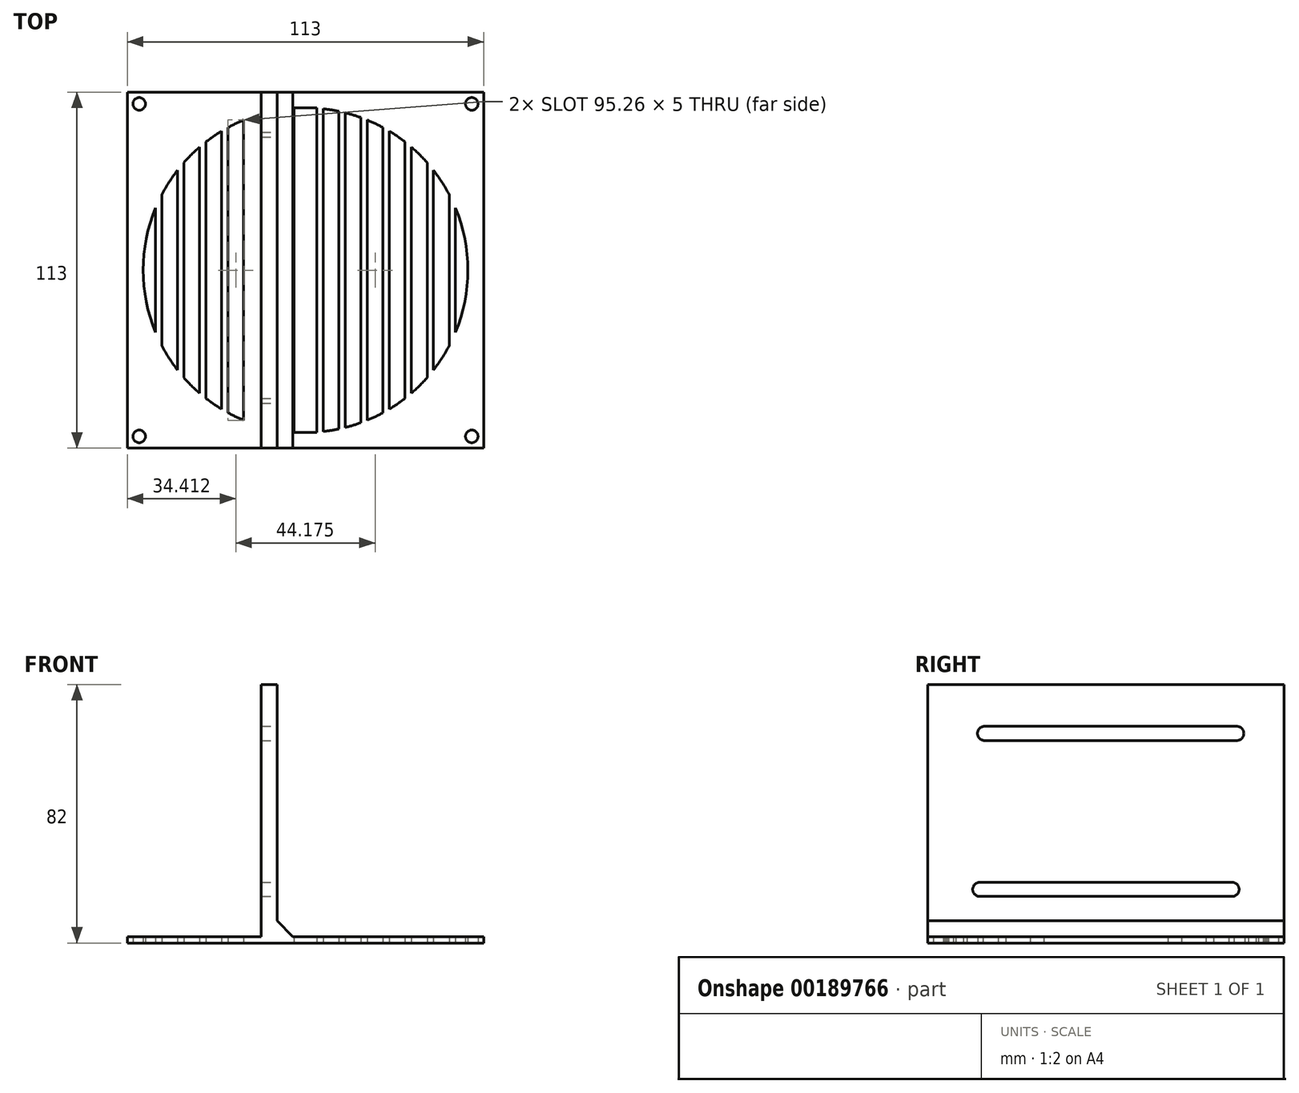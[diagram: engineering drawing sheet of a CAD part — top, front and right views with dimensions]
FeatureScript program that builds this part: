
annotation { "Feature Type Name" : "Feature", "Feature Type Description" : "" }
export const myFeature = defineFeature(function(context is Context, id is Id, definition is map)
    precondition{}
    {
        {
            var Q0;
            Q0=qCreatedBy(makeId("Top.planeOp"),FACE);
            var sketch = newSketch(context, id + "F0", { "sketchPlane" : qUnion([Q0])});
            skLineSegment(sketch, "E0.bottom", {"start": v(56.5, 56.5) * mm, "end": v(-56.5, 56.5) * mm});
            skLineSegment(sketch, "E0.top", {"start": v(56.5, -56.5) * mm, "end": v(-56.5, -56.5) * mm});
            skLineSegment(sketch, "E0.left", {"start": v(56.5, 56.5) * mm, "end": v(56.5, -56.5) * mm});
            skLineSegment(sketch, "E0.right", {"start": v(-56.5, 56.5) * mm, "end": v(-56.5, -56.5) * mm});
            skPoint(sketch, "E0.middle", {"position": v(0, 0) * mm});
            skCircle(sketch, "E1", {"center": v(-52.75, 52.75) * mm, "radius": 2 * mm});
            skCircle(sketch, "E2", {"center": v(52.75, 52.75) * mm, "radius": 2 * mm});
            skCircle(sketch, "E3", {"center": v(52.75, -52.75) * mm, "radius": 2 * mm});
            skCircle(sketch, "E4", {"center": v(-52.75, -52.75) * mm, "radius": 2 * mm});
            skLineSegment(sketch, "E5", {"start": v(-47.59, 19.69) * mm, "end": v(-47.59, -19.69) * mm});
            skLineSegment(sketch, "E6", {"start": v(-45.59, 23.96) * mm, "end": v(-45.59, -23.96) * mm});
            skLineSegment(sketch, "E7", {"start": v(-40.59, 31.7) * mm, "end": v(-40.59, -31.7) * mm});
            skLineSegment(sketch, "E8", {"start": v(-38.59, 34.1) * mm, "end": v(-38.59, -34.1) * mm});
            skLineSegment(sketch, "E9", {"start": v(-33.59, 39.04) * mm, "end": v(-33.59, -39.04) * mm});
            skLineSegment(sketch, "E10", {"start": v(-31.59, 40.68) * mm, "end": v(-31.59, -40.68) * mm});
            skLineSegment(sketch, "E11", {"start": v(-26.59, 44.1) * mm, "end": v(-26.59, -44.1) * mm});
            skLineSegment(sketch, "E12", {"start": v(-24.59, 45.25) * mm, "end": v(-24.59, -45.25) * mm});
            skLineSegment(sketch, "E13", {"start": v(-19.59, 47.63) * mm, "end": v(-19.59, -47.63) * mm});
            skLineSegment(sketch, "E14", {"start": v(-17.59, 48.4) * mm, "end": v(-17.59, -48.4) * mm});
            skLineSegment(sketch, "E15", {"start": v(-5.59, -51.2) * mm, "end": v(-5.59, 51.2) * mm});
            skLineSegment(sketch, "E16", {"start": v(0, 51.5) * mm, "end": v(0, -51.5) * mm});
            skPoint(sketch, "E16.endSnap0", {"position": v(0, -56.5) * mm});
            skArc(sketch, "E17.trimOffspring", {"start": v(-47.59, 19.69) * mm, "mid": v(-51.5, 0) * mm, "end": v(-47.59, -19.69) * mm});
            skArc(sketch, "E18.trimOffspring", {"start": v(-40.59, 31.7) * mm, "mid": v(-43.26, 27.94) * mm, "end": v(-45.59, 23.96) * mm});
            skArc(sketch, "E19.trimOffspring", {"start": v(-33.59, 39.04) * mm, "mid": v(-36.17, 36.66) * mm, "end": v(-38.59, 34.1) * mm});
            skArc(sketch, "E20.trimOffspring", {"start": v(-26.59, 44.1) * mm, "mid": v(-29.14, 42.46) * mm, "end": v(-31.59, 40.68) * mm});
            skArc(sketch, "E21.trimOffspring", {"start": v(-19.59, 47.63) * mm, "mid": v(-22.12, 46.5) * mm, "end": v(-24.59, 45.25) * mm});
            skArc(sketch, "E22.trimOffspring", {"start": v(-24.59, -45.25) * mm, "mid": v(-22.12, -46.5) * mm, "end": v(-19.59, -47.63) * mm});
            skArc(sketch, "E23.trimOffspring", {"start": v(-31.59, -40.68) * mm, "mid": v(-29.14, -42.46) * mm, "end": v(-26.59, -44.1) * mm});
            skArc(sketch, "E24.trimOffspring", {"start": v(-38.59, -34.1) * mm, "mid": v(-36.17, -36.66) * mm, "end": v(-33.59, -39.04) * mm});
            skArc(sketch, "E25.trimOffspring", {"start": v(-45.59, -23.96) * mm, "mid": v(-43.26, -27.94) * mm, "end": v(-40.59, -31.7) * mm});
            skArc(sketch, "E26.MirrorCS", {"start": v(26.59, 44.1) * mm, "mid": v(29.14, 42.46) * mm, "end": v(31.59, 40.68) * mm});
            skArc(sketch, "E27.MirrorCS", {"start": v(24.59, -45.25) * mm, "mid": v(22.12, -46.5) * mm, "end": v(19.59, -47.63) * mm});
            skArc(sketch, "E28.MirrorCS", {"start": v(33.59, 39.04) * mm, "mid": v(36.17, 36.66) * mm, "end": v(38.59, 34.1) * mm});
            skArc(sketch, "E29.MirrorCS", {"start": v(38.59, -34.1) * mm, "mid": v(36.17, -36.66) * mm, "end": v(33.59, -39.04) * mm});
            skArc(sketch, "E30.MirrorCS", {"start": v(17.59, -48.4) * mm, "mid": v(15.1, -49.23) * mm, "end": v(12.59, -49.94) * mm});
            skArc(sketch, "E31.MirrorCS", {"start": v(5.59, 51.2) * mm, "mid": v(8.1, 50.86) * mm, "end": v(10.59, 50.4) * mm});
            skArc(sketch, "E32.MirrorCS", {"start": v(10.59, -50.4) * mm, "mid": v(8.1, -50.86) * mm, "end": v(5.59, -51.2) * mm});
            skArc(sketch, "E33.MirrorCS", {"start": v(12.59, 49.94) * mm, "mid": v(15.1, 49.23) * mm, "end": v(17.59, 48.4) * mm});
            skArc(sketch, "E34.MirrorCS", {"start": v(31.59, -40.68) * mm, "mid": v(29.14, -42.46) * mm, "end": v(26.59, -44.1) * mm});
            skArc(sketch, "E35.MirrorCS", {"start": v(19.59, 47.63) * mm, "mid": v(22.12, 46.5) * mm, "end": v(24.59, 45.25) * mm});
            skArc(sketch, "E36.MirrorCS", {"start": v(45.59, -23.96) * mm, "mid": v(43.26, -27.94) * mm, "end": v(40.59, -31.7) * mm});
            skLineSegment(sketch, "E37.MirrorCS", {"start": v(12.59, 49.94) * mm, "end": v(12.59, -49.94) * mm});
            skLineSegment(sketch, "E38.MirrorCS", {"start": v(17.59, 48.4) * mm, "end": v(17.59, -48.4) * mm});
            skLineSegment(sketch, "E39.MirrorCS", {"start": v(33.59, 39.04) * mm, "end": v(33.59, -39.04) * mm});
            skLineSegment(sketch, "E40.MirrorCS", {"start": v(31.59, 40.68) * mm, "end": v(31.59, -40.68) * mm});
            skLineSegment(sketch, "E41.MirrorCS", {"start": v(26.59, 44.1) * mm, "end": v(26.59, -44.1) * mm});
            skLineSegment(sketch, "E42.MirrorCS", {"start": v(38.59, 34.1) * mm, "end": v(38.59, -34.1) * mm});
            skLineSegment(sketch, "E43.MirrorCS", {"start": v(40.59, 31.7) * mm, "end": v(40.59, -31.7) * mm});
            skLineSegment(sketch, "E44.MirrorCS", {"start": v(45.59, 23.96) * mm, "end": v(45.59, -23.96) * mm});
            skLineSegment(sketch, "E45.MirrorCS", {"start": v(47.59, 19.69) * mm, "end": v(47.59, -19.69) * mm});
            skLineSegment(sketch, "E46.MirrorCS", {"start": v(5.59, -51.2) * mm, "end": v(5.59, 51.2) * mm});
            skLineSegment(sketch, "E47.MirrorCS", {"start": v(19.59, 47.63) * mm, "end": v(19.59, -47.63) * mm});
            skArc(sketch, "E48.MirrorCS", {"start": v(40.59, 31.7) * mm, "mid": v(43.26, 27.94) * mm, "end": v(45.59, 23.96) * mm});
            skLineSegment(sketch, "E49.MirrorCS", {"start": v(10.59, 50.4) * mm, "end": v(10.59, -50.4) * mm});
            skLineSegment(sketch, "E50.MirrorCS", {"start": v(24.59, 45.25) * mm, "end": v(24.59, -45.25) * mm});
            skArc(sketch, "E51.MirrorCS", {"start": v(47.59, 19.69) * mm, "mid": v(51.5, 0) * mm, "end": v(47.59, -19.69) * mm});
            skLineSegment(sketch, "E52.bottom", {"start": v(-3.59, 51.52) * mm, "end": v(3.59, 51.52) * mm});
            skLineSegment(sketch, "E52.top", {"start": v(-3.59, -51.52) * mm, "end": v(3.59, -51.52) * mm});
            skLineSegment(sketch, "E52.left", {"start": v(-3.59, 51.52) * mm, "end": v(-3.59, -51.52) * mm});
            skLineSegment(sketch, "E52.right", {"start": v(3.59, 51.52) * mm, "end": v(3.59, -51.52) * mm});
            skSolve(sketch);
        }
        {
            var Q0;
            Q0=makeQuery(id+"F0.imprint","IMPRINT",FACE,{"disambiguationData":[TD([[makeQuery(id+"F0.imprint","IMPRINT",EDGE,{"derivedFrom":sQuery(id+"F0.wireOp",EDGE,"E0.bottom")}),1.0]])]});
            extrude(context, id + "F1", {"entities" : qUnion([Q0]), "depth" : 2 * mm});
        }
        {
            var Q0;
            Q0=makeQuery(id+"F1.opExtrude","CAP_FACE",FACE,{"disambiguationData":[OSD([sQuery(id+"F0.wireOp",EDGE,"E0.bottom"),sQuery(id+"F0.wireOp",EDGE,"E0.top"),sQuery(id+"F0.wireOp",EDGE,"E0.left"),sQuery(id+"F0.wireOp",EDGE,"E0.right"),sQuery(id+"F0.wireOp",EDGE,"E1"),sQuery(id+"F0.wireOp",EDGE,"E3"),sQuery(id+"F0.wireOp",EDGE,"E4"),sQuery(id+"F0.wireOp",EDGE,"E5"),sQuery(id+"F0.wireOp",EDGE,"E6"),sQuery(id+"F0.wireOp",EDGE,"E7"),sQuery(id+"F0.wireOp",EDGE,"E8"),sQuery(id+"F0.wireOp",EDGE,"E9"),sQuery(id+"F0.wireOp",EDGE,"E10"),sQuery(id+"F0.wireOp",EDGE,"E11"),sQuery(id+"F0.wireOp",EDGE,"E12"),sQuery(id+"F0.wireOp",EDGE,"E13"),sQuery(id+"F0.wireOp",EDGE,"E17.trimOffspring"),sQuery(id+"F0.wireOp",EDGE,"E18.trimOffspring"),sQuery(id+"F0.wireOp",EDGE,"E19.trimOffspring"),sQuery(id+"F0.wireOp",EDGE,"E20.trimOffspring"),sQuery(id+"F0.wireOp",EDGE,"E21.trimOffspring"),sQuery(id+"F0.wireOp",EDGE,"E22.trimOffspring"),sQuery(id+"F0.wireOp",EDGE,"E23.trimOffspring"),sQuery(id+"F0.wireOp",EDGE,"E24.trimOffspring"),sQuery(id+"F0.wireOp",EDGE,"E25.trimOffspring"),sQuery(id+"F0.wireOp",EDGE,"E26.MirrorCS"),sQuery(id+"F0.wireOp",EDGE,"E27.MirrorCS"),sQuery(id+"F0.wireOp",EDGE,"E28.MirrorCS"),sQuery(id+"F0.wireOp",EDGE,"E29.MirrorCS"),sQuery(id+"F0.wireOp",EDGE,"E30.MirrorCS"),sQuery(id+"F0.wireOp",EDGE,"E31.MirrorCS"),sQuery(id+"F0.wireOp",EDGE,"E32.MirrorCS"),sQuery(id+"F0.wireOp",EDGE,"E33.MirrorCS"),sQuery(id+"F0.wireOp",EDGE,"E34.MirrorCS"),sQuery(id+"F0.wireOp",EDGE,"E35.MirrorCS"),sQuery(id+"F0.wireOp",EDGE,"E2"),sQuery(id+"F0.wireOp",EDGE,"E36.MirrorCS"),sQuery(id+"F0.wireOp",EDGE,"E37.MirrorCS"),sQuery(id+"F0.wireOp",EDGE,"E38.MirrorCS"),sQuery(id+"F0.wireOp",EDGE,"E39.MirrorCS"),sQuery(id+"F0.wireOp",EDGE,"E40.MirrorCS"),sQuery(id+"F0.wireOp",EDGE,"E41.MirrorCS"),sQuery(id+"F0.wireOp",EDGE,"E42.MirrorCS"),sQuery(id+"F0.wireOp",EDGE,"E43.MirrorCS"),sQuery(id+"F0.wireOp",EDGE,"E44.MirrorCS"),sQuery(id+"F0.wireOp",EDGE,"E45.MirrorCS"),sQuery(id+"F0.wireOp",EDGE,"E46.MirrorCS"),sQuery(id+"F0.wireOp",EDGE,"E47.MirrorCS"),sQuery(id+"F0.wireOp",EDGE,"E48.MirrorCS"),sQuery(id+"F0.wireOp",EDGE,"E49.MirrorCS"),sQuery(id+"F0.wireOp",EDGE,"E50.MirrorCS"),sQuery(id+"F0.wireOp",EDGE,"E51.MirrorCS"),sQuery(id+"F0.wireOp",EDGE,"E52.bottom"),sQuery(id+"F0.wireOp",EDGE,"E52.top"),sQuery(id+"F0.wireOp",EDGE,"E52.left"),sQuery(id+"F0.wireOp",EDGE,"E52.right")])],"isStart":false});
            var sketch = newSketch(context, id + "F2", { "sketchPlane" : qUnion([Q0])});
            skLineSegment(sketch, "E53.bottom", {"start": v(-14, 56.5) * mm, "end": v(-9, 56.5) * mm});
            skLineSegment(sketch, "E53.top", {"start": v(-14, -56.5) * mm, "end": v(-9, -56.5) * mm});
            skLineSegment(sketch, "E53.left", {"start": v(-14, 56.5) * mm, "end": v(-14, -56.5) * mm});
            skLineSegment(sketch, "E53.right", {"start": v(-9, 56.5) * mm, "end": v(-9, -56.5) * mm});
            skPoint(sketch, "E53.middle", {"position": v(-11.5, 0) * mm});
            skSolve(sketch);
        }
        {
            var Q0;
            Q0 = qSketchRegion(id + "F2", true);
            extrude(context, id + "F3", {"entities" : qUnion([Q0]), "operationType" : NewBodyOperationType.ADD, "depth" : 80 * mm});
        }
        {
            var Q0;
            Q0=makeQuery(id+"F3.opExtrude","SWEPT_FACE",FACE,{"disambiguationData":[OSD([sQuery(id+"F2.wireOp",EDGE,"E53.right")])]});
            var sketch = newSketch(context, id + "F4", { "sketchPlane" : qUnion([Q0])});
            skArc(sketch, "E54", {"start": v(-40, 19.25) * mm, "mid": v(-42.25, 17) * mm, "end": v(-40, 14.75) * mm});
            skArc(sketch, "E55", {"start": v(40, 14.75) * mm, "mid": v(42.25, 17) * mm, "end": v(40, 19.25) * mm});
            skLineSegment(sketch, "E56", {"start": v(-35.5, 14.75) * mm, "end": v(-35.5, 14.75) * mm});
            skLineSegment(sketch, "E57", {"start": v(35.5, 19.25) * mm, "end": v(35.5, 19.25) * mm});
            skLineSegment(sketch, "E58", {"start": v(-40, 19.25) * mm, "end": v(-35.5, 19.25) * mm});
            skLineSegment(sketch, "E59", {"start": v(-40, 14.75) * mm, "end": v(-35.5, 14.75) * mm});
            skLineSegment(sketch, "E60", {"start": v(35.5, 19.25) * mm, "end": v(40, 19.25) * mm});
            skLineSegment(sketch, "E61", {"start": v(35.5, 14.75) * mm, "end": v(40, 14.75) * mm});
            skArc(sketch, "E62", {"start": v(-38.5, 68.75) * mm, "mid": v(-40.75, 66.5) * mm, "end": v(-38.5, 64.25) * mm});
            skArc(sketch, "E63", {"start": v(41.5, 64.25) * mm, "mid": v(43.75, 66.5) * mm, "end": v(41.5, 68.75) * mm});
            skLineSegment(sketch, "E64", {"start": v(-38.5, 68.75) * mm, "end": v(-34.5, 68.75) * mm});
            skLineSegment(sketch, "E65", {"start": v(-38.5, 64.25) * mm, "end": v(-34.5, 64.25) * mm});
            skLineSegment(sketch, "E66", {"start": v(34.5, 68.75) * mm, "end": v(41.5, 68.75) * mm});
            skLineSegment(sketch, "E67", {"start": v(34.5, 64.25) * mm, "end": v(41.5, 64.25) * mm});
            skLineSegment(sketch, "E68", {"start": v(-35.5, 19.25) * mm, "end": v(35.5, 19.25) * mm});
            skLineSegment(sketch, "E69", {"start": v(-35.5, 14.75) * mm, "end": v(35.5, 14.75) * mm});
            skLineSegment(sketch, "E70", {"start": v(-34.5, 68.75) * mm, "end": v(34.5, 68.75) * mm});
            skLineSegment(sketch, "E71", {"start": v(-34.5, 64.25) * mm, "end": v(34.5, 64.25) * mm});
            skPoint(sketch, "E72.center.orphan", {"position": v(-34.5, 66.5) * mm});
            skPoint(sketch, "E73.center.orphan", {"position": v(34.5, 66.5) * mm});
            skSolve(sketch);
        }
        {
            var Q0;
            Q0 = qSketchRegion(id + "F4", true);
            extrude(context, id + "F5", {"entities" : qUnion([Q0]), "operationType" : NewBodyOperationType.REMOVE, "oppositeDirection" : true, "depth" : 25 * mm});
        }
        {
            var Q0;
            Q0=makeQuery(id+"F3.opExtrude","CAP_EDGE",EDGE,{"disambiguationData":[OSD([sQuery(id+"F2.wireOp",EDGE,"E53.right")])],"isStart":true});
            var Q1;
            Q1=makeQuery(id+"F3.opExtrude","CAP_EDGE",EDGE,{"disambiguationData":[OSD([sQuery(id+"F2.wireOp",EDGE,"E53.left")])],"isStart":true});
            chamfer(context, id + "F6", {"entities" : qUnion([Q0, Q1]), "width" : 5 * mm, "tangentPropagation" : true});
        }
    });
